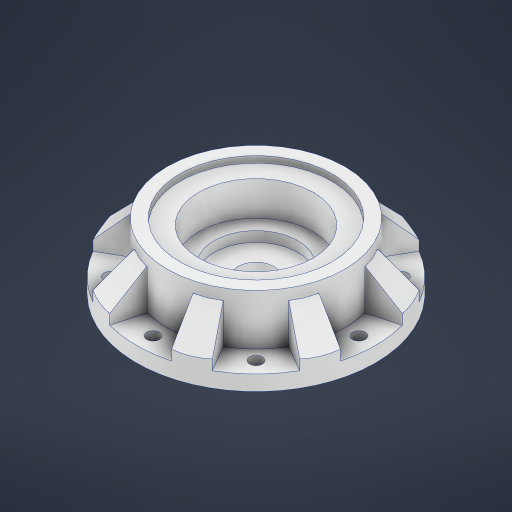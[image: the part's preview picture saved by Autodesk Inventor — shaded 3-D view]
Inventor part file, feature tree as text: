
AUTODESK INVENTOR PART (.ipt)
format: ipt  version: 2024 (Build 280153000, 153)  size: 512,000 bytes
history: native  units: mm
features: extrude x9, sketch x9, pattern_circular x2, chamfer x1, projected_geometry x1
ambient origin geometry x8: Origin, YZ Plane, XZ Plane, XY Plane, X Axis, Y Axis, Z Axis, Center Point
bodies: Solid1 (feature_tree)
feature tree (22):
  extrude  "Extrusion1"  Depth=12.0mm TaperAngle=0.0deg
  extrude  "Extrusion2"  Depth=10.0mm TaperAngle=0.0deg
  extrude  "Extrusion3"  Depth=90.0mm
  pattern_circular  "Circular Pattern1"  Count=14  [1 undecoded]
  extrude  "Extrusion4"  Depth=5.0mm TaperAngle=0.0deg
  extrude  "Extrusion5"  Depth=80.0mm TaperAngle=360.0deg
  extrude  "Extrusion6"  TaperAngle=15.0deg  [1 undecoded]
  extrude  "Extrusion7"  Depth=1.308997mm
  extrude  "Extrusion8"  Depth=31.5mm TaperAngle=0.0deg
  chamfer  "Chamfer1"  Distance=31.5mm Angle=45.0deg
  pattern_circular  "Circular Pattern2"  Count=8 Angle=360.0deg
  extrude  "Extrusion10"  [1 undecoded]
  sketch  "Sketch1"  dims[d0=250.0mm d1=12.0mm d2=0.0mm]
  sketch  "Sketch2"  dims[d3=40.0mm d4=0.0mm d5=10.0mm d6=0.0mm]
  projected_geometry  "Projected Loop1"
  sketch  "Sketch3"  dims[d7=1800.0mm d8=360.0deg d10=90.0mm d11=140.0mm]
  sketch  "Sketch4"  dims[d12=8.0mm d13=0.0mm d14=5.0mm d15=0.0mm]
  sketch  "Sketch5"  dims[d16=25.0mm d17=0.0mm d18=80.0mm d20=360.0deg]
  sketch  "Sketch6"  dims[d22=20.0mm d23=0.0mm d24=15.0deg]
  sketch  "Sketch7"  dims[d25=60.0deg d26=1.308997mm]
  sketch  "Sketch8"  dims[d27=1.308997mm d28=31.5mm d29=0.0mm d30=31.5mm d31=2.0mm d32=45.0deg d33=80.0mm d34=360.0deg]
  sketch  "Sketch10"  dims[d38=100.0mm d39=0.0mm]
note: 3 required parameter values undecoded (feature->parameter linkage not recoverable at this tier; creation-order binding heuristic only, values carry confidence <= 0.55)
